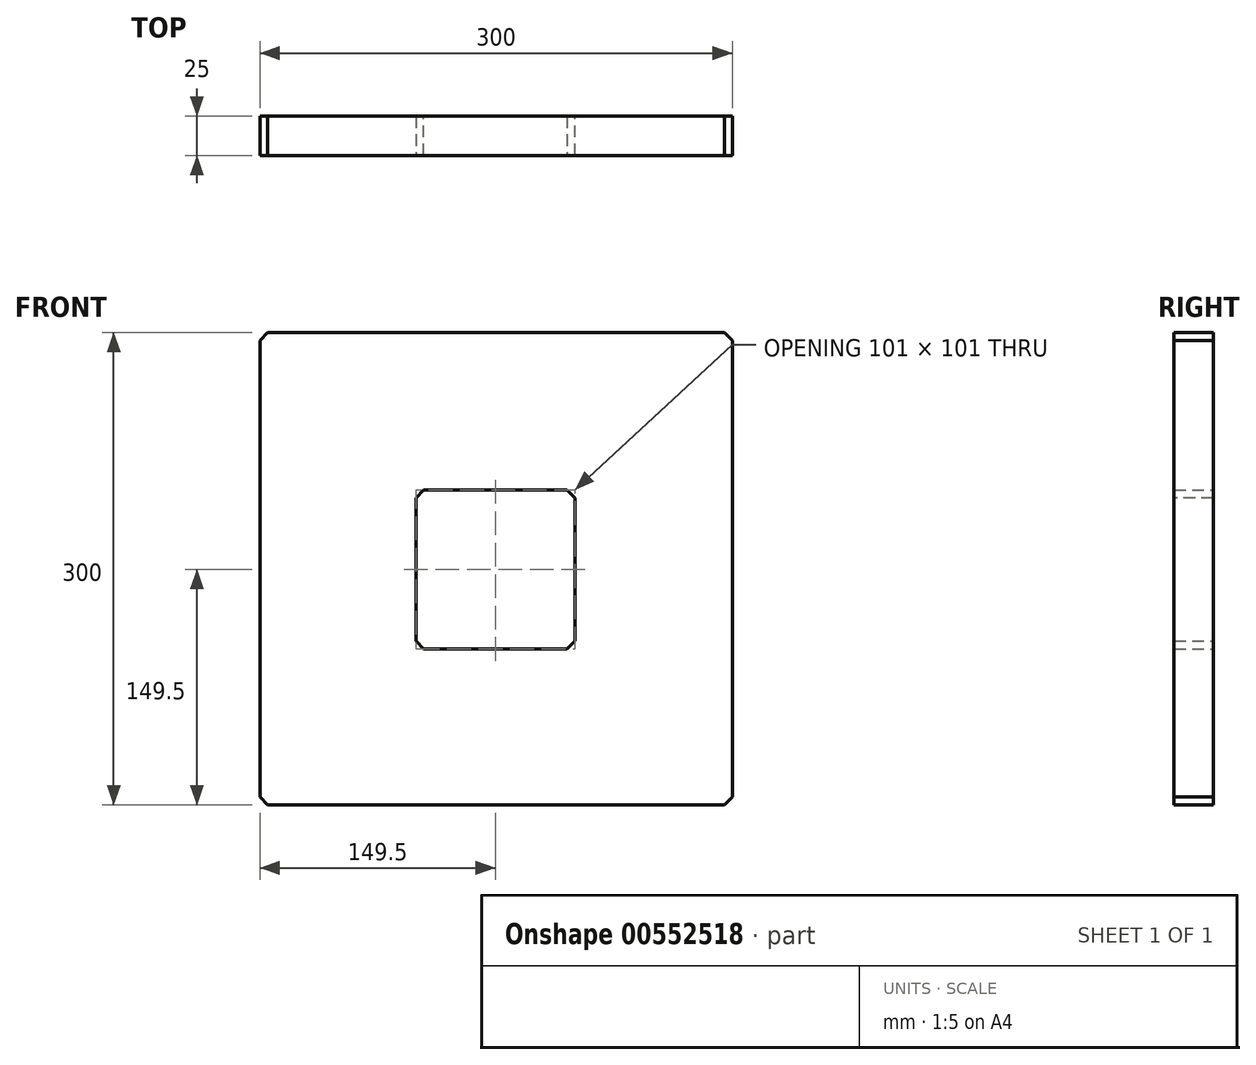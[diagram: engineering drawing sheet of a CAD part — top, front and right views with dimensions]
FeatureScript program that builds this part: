
annotation { "Feature Type Name" : "Feature", "Feature Type Description" : "" }
export const myFeature = defineFeature(function(context is Context, id is Id, definition is map)
    precondition{}
    {
        {
            var Q0;
            Q0=qCreatedBy(makeId("Front.planeOp"),FACE);
            var sketch = newSketch(context, id + "F0", { "sketchPlane" : qUnion([Q0])});
            skLineSegment(sketch, "E0.bottom", {"start": v(0, 0) * mm, "end": v(300, 0) * mm});
            skLineSegment(sketch, "E0.top", {"start": v(0, -300) * mm, "end": v(300, -300) * mm});
            skLineSegment(sketch, "E0.left", {"start": v(0, 0) * mm, "end": v(0, -300) * mm});
            skLineSegment(sketch, "E0.right", {"start": v(300, 0) * mm, "end": v(300, -300) * mm});
            skLineSegment(sketch, "E1.bottom", {"start": v(99, -100) * mm, "end": v(200, -100) * mm});
            skLineSegment(sketch, "E1.top", {"start": v(99, -201) * mm, "end": v(200, -201) * mm});
            skLineSegment(sketch, "E1.left", {"start": v(99, -100) * mm, "end": v(99, -201) * mm});
            skLineSegment(sketch, "E1.right", {"start": v(200, -100) * mm, "end": v(200, -201) * mm});
            skSolve(sketch);
        }
        {
            var Q0;
            Q0=makeQuery(id+"F0.imprint","IMPRINT",FACE,{"disambiguationData":[TD([[makeQuery(id+"F0.imprint","IMPRINT",EDGE,{"derivedFrom":sQuery(id+"F0.wireOp",EDGE,"E0.bottom")}),-1.0]])]});
            extrude(context, id + "F1", {"entities" : qUnion([Q0]), "depth" : 25 * mm, "offsetDistance" : 25 * mm});
        }
        {
            var Q0;
            Q0=makeQuery(id+"F1.opExtrude","SWEPT_EDGE",EDGE,{"disambiguationData":[OSD([sQuery(id+"F0.wireOp",EDGE,"E0.top"),sQuery(id+"F0.wireOp",EDGE,"E0.left")])]});
            var Q1;
            Q1=makeQuery(id+"F1.opExtrude","SWEPT_EDGE",EDGE,{"disambiguationData":[OSD([sQuery(id+"F0.wireOp",EDGE,"E0.top"),sQuery(id+"F0.wireOp",EDGE,"E0.right")])]});
            var Q2;
            Q2=makeQuery(id+"F1.opExtrude","SWEPT_EDGE",EDGE,{"disambiguationData":[OSD([sQuery(id+"F0.wireOp",EDGE,"E0.bottom"),sQuery(id+"F0.wireOp",EDGE,"E0.right")])]});
            var Q3;
            Q3=makeQuery(id+"F1.opExtrude","SWEPT_EDGE",EDGE,{"disambiguationData":[OSD([sQuery(id+"F0.wireOp",EDGE,"E0.bottom"),sQuery(id+"F0.wireOp",EDGE,"E0.left")])]});
            var Q4;
            Q4=makeQuery(id+"F1.opExtrude","SWEPT_EDGE",EDGE,{"disambiguationData":[OSD([sQuery(id+"F0.wireOp",EDGE,"E1.top"),sQuery(id+"F0.wireOp",EDGE,"E1.right")])]});
            var Q5;
            Q5=makeQuery(id+"F1.opExtrude","SWEPT_EDGE",EDGE,{"disambiguationData":[OSD([sQuery(id+"F0.wireOp",EDGE,"E1.bottom"),sQuery(id+"F0.wireOp",EDGE,"E1.right")])]});
            var Q6;
            Q6=makeQuery(id+"F1.opExtrude","SWEPT_EDGE",EDGE,{"disambiguationData":[OSD([sQuery(id+"F0.wireOp",EDGE,"E1.bottom"),sQuery(id+"F0.wireOp",EDGE,"E1.left")])]});
            var Q7;
            Q7=makeQuery(id+"F1.opExtrude","SWEPT_EDGE",EDGE,{"disambiguationData":[OSD([sQuery(id+"F0.wireOp",EDGE,"E1.top"),sQuery(id+"F0.wireOp",EDGE,"E1.left")])]});
            chamfer(context, id + "F2", {"entities" : qUnion([Q0, Q1, Q2, Q3, Q4, Q5, Q6, Q7]), "width" : 5 * mm, "tangentPropagation" : true});
        }
    });
